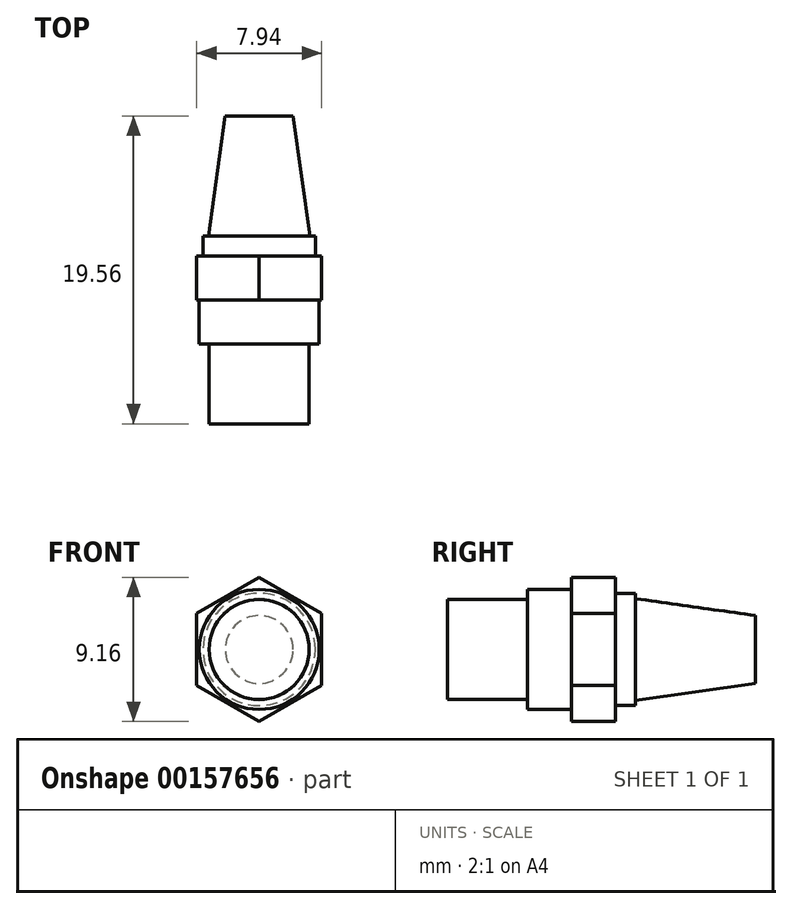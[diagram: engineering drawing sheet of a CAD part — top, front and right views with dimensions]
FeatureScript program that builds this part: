
annotation { "Feature Type Name" : "Feature", "Feature Type Description" : "" }
export const myFeature = defineFeature(function(context is Context, id is Id, definition is map)
    precondition{}
    {
        {
            var Q0;
            Q0=qCreatedBy(makeId("Front.planeOp"),FACE);
            var sketch = newSketch(context, id + "F0", { "sketchPlane" : qUnion([Q0])});
            skLineSegment(sketch, "E0.0", {"start": v(3.97, 2.3) * mm, "end": v(3.97, -2.3) * mm});
            skLineSegment(sketch, "E0.1", {"start": v(3.97, -2.3) * mm, "end": v(0, -4.58) * mm});
            skLineSegment(sketch, "E0.2", {"start": v(0, -4.58) * mm, "end": v(-3.97, -2.3) * mm});
            skLineSegment(sketch, "E0.3", {"start": v(-3.97, -2.3) * mm, "end": v(-3.97, 2.3) * mm});
            skLineSegment(sketch, "E0.4", {"start": v(-3.97, 2.3) * mm, "end": v(0, 4.58) * mm});
            skLineSegment(sketch, "E0.5", {"start": v(0, 4.58) * mm, "end": v(3.97, 2.3) * mm});
            skPoint(sketch, "E0.0.midPoint", {"position": v(3.97, 0) * mm});
            skSolve(sketch);
        }
        {
            var Q0;
            Q0=makeQuery(id+"F0.imprint","IMPRINT",FACE,{"disambiguationData":[TD([[makeQuery(id+"F0.imprint","IMPRINT",EDGE,{"derivedFrom":sQuery(id+"F0.wireOp",EDGE,"E0.0")}),-1.0]])]});
            extrude(context, id + "F1", {"entities" : qUnion([Q0]), "depth" : 2.8 * mm});
        }
        {
            var Q0;
            Q0=makeQuery(id+"F1.opExtrude","CAP_FACE",FACE,{"disambiguationData":[OSD([sQuery(id+"F0.wireOp",EDGE,"E0.0"),sQuery(id+"F0.wireOp",EDGE,"E0.1"),sQuery(id+"F0.wireOp",EDGE,"E0.2"),sQuery(id+"F0.wireOp",EDGE,"E0.3"),sQuery(id+"F0.wireOp",EDGE,"E0.4"),sQuery(id+"F0.wireOp",EDGE,"E0.5")])],"isStart":false});
            var sketch = newSketch(context, id + "F2", { "sketchPlane" : qUnion([Q0])});
            skCircle(sketch, "E1", {"center": v(0, 0) * mm, "radius": 3.81 * mm});
            skSolve(sketch);
        }
        {
            var Q0;
            Q0=makeQuery(id+"F2.imprint","IMPRINT",FACE,{"disambiguationData":[TD([[makeQuery(id+"F2.imprint","IMPRINT",EDGE,{"derivedFrom":sQuery(id+"F2.wireOp",EDGE,"E1")}),1.0]])]});
            extrude(context, id + "F3", {"entities" : qUnion([Q0]), "operationType" : NewBodyOperationType.ADD, "depth" : 2.8 * mm});
        }
        {
            var Q0;
            Q0=makeQuery(id+"F3.opExtrude","CAP_FACE",FACE,{"disambiguationData":[OSD([sQuery(id+"F2.wireOp",EDGE,"E1")])],"isStart":false});
            var sketch = newSketch(context, id + "F4", { "sketchPlane" : qUnion([Q0])});
            skCircle(sketch, "E2", {"center": v(0, 0) * mm, "radius": 3.18 * mm});
            skSolve(sketch);
        }
        {
            var Q0;
            Q0=makeQuery(id+"F4.imprint","IMPRINT",FACE,{"disambiguationData":[TD([[makeQuery(id+"F4.imprint","IMPRINT",EDGE,{"derivedFrom":sQuery(id+"F4.wireOp",EDGE,"E2")}),1.0]])]});
            extrude(context, id + "F5", {"entities" : qUnion([Q0]), "operationType" : NewBodyOperationType.ADD, "depth" : 5.08 * mm});
        }
        {
            var Q0;
            Q0=makeQuery(id+"F1.opExtrude","CAP_FACE",FACE,{"disambiguationData":[OSD([sQuery(id+"F0.wireOp",EDGE,"E0.0"),sQuery(id+"F0.wireOp",EDGE,"E0.1"),sQuery(id+"F0.wireOp",EDGE,"E0.2"),sQuery(id+"F0.wireOp",EDGE,"E0.3"),sQuery(id+"F0.wireOp",EDGE,"E0.4"),sQuery(id+"F0.wireOp",EDGE,"E0.5")])],"isStart":true});
            var sketch = newSketch(context, id + "F6", { "sketchPlane" : qUnion([Q0])});
            skCircle(sketch, "E3", {"center": v(0, 0) * mm, "radius": 3.56 * mm});
            skSolve(sketch);
        }
        {
            var Q0;
            Q0=makeQuery(id+"F6.imprint","IMPRINT",FACE,{"disambiguationData":[TD([[makeQuery(id+"F6.imprint","IMPRINT",EDGE,{"derivedFrom":sQuery(id+"F6.wireOp",EDGE,"E3")}),1.0]])]});
            extrude(context, id + "F7", {"entities" : qUnion([Q0]), "operationType" : NewBodyOperationType.ADD, "depth" : 1.27 * mm});
        }
        {
            var Q0;
            Q0=makeQuery(id+"F7.opExtrude","CAP_FACE",FACE,{"disambiguationData":[OSD([sQuery(id+"F6.wireOp",EDGE,"E3")])],"isStart":false});
            var sketch = newSketch(context, id + "F8", { "sketchPlane" : qUnion([Q0])});
            skCircle(sketch, "E4", {"center": v(0, 0) * mm, "radius": 3.22 * mm});
            skSolve(sketch);
        }
        {
            var Q0;
            Q0=makeQuery(id+"F8.imprint","IMPRINT",FACE,{"disambiguationData":[TD([[makeQuery(id+"F8.imprint","IMPRINT",EDGE,{"derivedFrom":sQuery(id+"F8.wireOp",EDGE,"E4")}),1.0]])]});
            extrude(context, id + "F9", {"entities" : qUnion([Q0]), "operationType" : NewBodyOperationType.ADD, "depth" : 7.62 * mm, "hasDraft" : true, "draftAngle" : 8 * degree, "draftPullDirection" : true});
        }
    });
